# Revit family: calido_clickbeam_maxi_742165_003_1ec0
name_source: partatom
category: Lighting Fixtures
units: mm (PartAtom-declared; Revit-internal decimal feet)

## family parameters
Cut with Voids When Loaded = No
Host = Face
Light Source = No
Part Type = Normal
Room Calculation Point = No
Round Connector Dimension = Use Diameter
Shared = No

## types (1)
- Clickbeam Spot (1 x LED Modul 830, 2700 lm, 3000)
    Apparent Load = 26 VA
    CIE Flux Codes = 96 100 100 100 100
    Color Rendering = 80
    Color Temperature = 3000
    Default Elevation = 1800 mm
    Description = Series: CALIDO CLICKBEAM maxi D90
LED surface-mounted projector with modern cylindrical design with no visible cooling ribs. Housing: die cast aluminium and sheet steel, powder-coated. Track-in driver integrated into the adapter. Rotation range: 356°. Swivel range: 90°. Front ring die-cast aluminium black. Hybrid optical system with polycarbonate lens and reflector in faceted aluminium for particularly homogeneous lighting. Special Click Beam lens suitable for different beam angles. Adjustable lens position by means of push mechanism to adjust the beam angle. Black front ring to prevent glare from the side. UVA- and IR-free light. With multi adaptor for 3-circuit tracks 230 V. Suitable for Track on ceiling. Converter integrated in the adapter. The following accessories can be mounted without use of tools: honeycomb louvre. 
Colour: deep black, matt (RAL 9005)
Diameter: 90 mm
Height: 162 mm
Lamp: LED
Socket: without socket
Colour temperature: 3000K
Colour rendering index (CRI): 80
System power: 26 W
Rated luminous flux: 2700 lm
Luminous efficiency: 104 lm/W
System power 2: 26 W
Rated luminous flux 2: 2900 lm
Luminous efficiency 2: 112 lm/W
Control gear: Regulated power supply
Protection class: I
Type of protection: IP 20
    Height = 162 mm
    Lamp = 1 x LED Modul 830
    Lamp Light Flux = 2700 lm
    Lamp count = 1
    Length = 90 mm
    Lifetime = 50000 h
    Luminous efficacy = 104 lm/W
    Manufacturer = RZB
    ModVariant = No
    Model = 742165.003
    Mounting Place = Ceiling
    Mounting Type = Surface mounted
    Number of Poles = 1
    OnlyDefault = Yes
    Power Factor = 1
    Product Name = CALIDO CLICKBEAM maxi
    Product group = Track mounted projectors
    ProductGroupID = 301
    Protection Class = Protection class I
    Protection Degree = IP 20
    RLX_Detail_Level = 1
    RLX_Emergency_Light_Flux = 0 lm
    RLX_Emergency_Type = 0
    RLX_Emergency_Type_DB = No
    RlxData = <blob elided: 43133 chars, md5=29ce7a45>
    Socket = socket
    Standby Power = 0 W
    System Light Flux = 2700 lm
    System Power = 26 W
    Type Comments = Clickbeam Spot
    Type Image = 742165.003.jpg
    URL = http://relux.com
    VarID = clickbeam_spot
    Voltage = 0 V
    Weight = 0.00 kg
    Width = 0 mm  [stored 0 ft]

note: [stored X ft] marks values corroborated as IEEE doubles in the binary element streams (Revit-internal decimal feet)

## geometry (parser evidence)
native form markers: Sweep x13
no freeform markers — native parametric forms only
